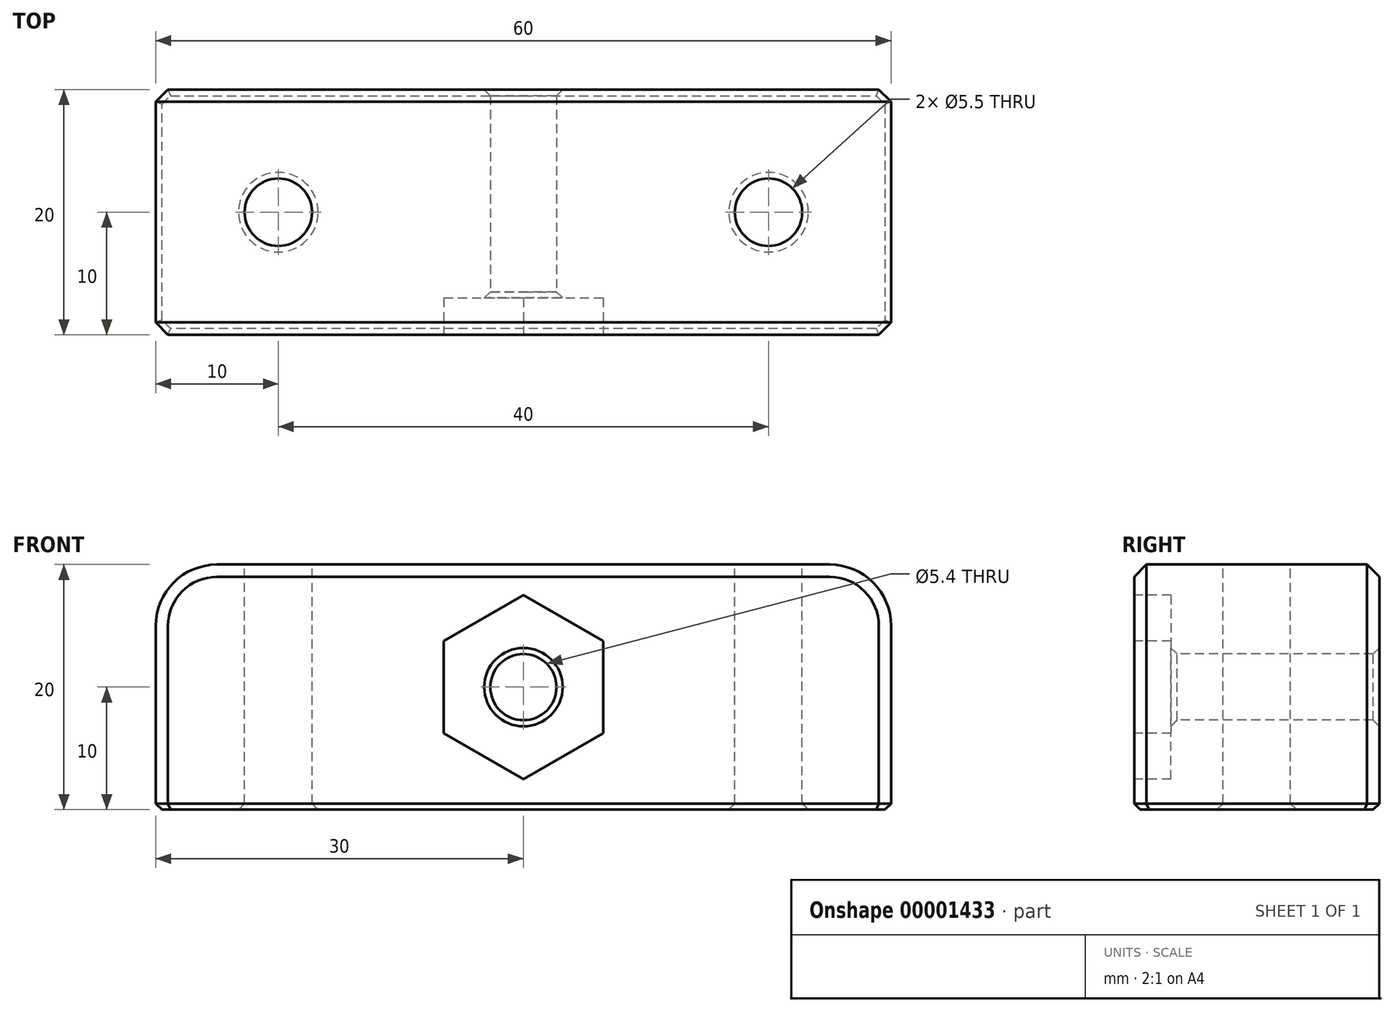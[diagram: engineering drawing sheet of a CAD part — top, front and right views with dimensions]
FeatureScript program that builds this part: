
annotation { "Feature Type Name" : "Feature", "Feature Type Description" : "" }
export const myFeature = defineFeature(function(context is Context, id is Id, definition is map)
    precondition{}
    {
        {
            var Q0;
            Q0=qCreatedBy(makeId("Top.planeOp"),FACE);
            var sketch = newSketch(context, id + "F0", { "sketchPlane" : qUnion([Q0])});
            skLineSegment(sketch, "E0.rect.bottom", {"start": v(30, 10) * mm, "end": v(-30, 10) * mm});
            skLineSegment(sketch, "E0.rect.top", {"start": v(30, -10) * mm, "end": v(-30, -10) * mm});
            skLineSegment(sketch, "E0.rect.left", {"start": v(30, 10) * mm, "end": v(30, -10) * mm});
            skLineSegment(sketch, "E0.rect.right", {"start": v(-30, 10) * mm, "end": v(-30, -10) * mm});
            skPoint(sketch, "E0.rect.middle", {"position": v(0, 0) * mm});
            skSolve(sketch);
        }
        {
            var Q0;
            Q0=makeQuery(id+"F0.imprint","IMPRINT",FACE,{"disambiguationData":[TD([[makeQuery(id+"F0.imprint","IMPRINT",EDGE,{"derivedFrom":sQuery(id+"F0.wireOp",EDGE,"E0.rect.bottom")}),1.0]])]});
            extrude(context, id + "F1", {"entities" : qUnion([Q0]), "depth" : 20 * mm});
        }
        {
            var Q0;
            Q0=makeQuery(id+"F1.opExtrude","SWEPT_FACE",FACE,{"disambiguationData":[OSD([sQuery(id+"F0.wireOp",EDGE,"E0.rect.top")])]});
            var sketch = newSketch(context, id + "F2", { "sketchPlane" : qUnion([Q0])});
            skLineSegment(sketch, "E1", {"start": v(0, 0) * mm, "end": v(0, 20) * mm, "construction": true});
            skCircle(sketch, "E2", {"center": v(0, 10) * mm, "radius": 2.7 * mm});
            skSolve(sketch);
        }
        {
            var Q0;
            Q0=makeQuery(id+"F2.imprint","IMPRINT",FACE,{"disambiguationData":[TD([[makeQuery(id+"F2.imprint","IMPRINT",EDGE,{"derivedFrom":sQuery(id+"F2.wireOp",EDGE,"E2")}),1.0]])]});
            extrude(context, id + "F3", {"entities" : qUnion([Q0]), "operationType" : NewBodyOperationType.REMOVE, "endBound" : BoundingType.THROUGH_ALL, "oppositeDirection" : true, "depth" : 25 * mm});
        }
        {
            var Q0;
            Q0=makeQuery(id+"F1.opExtrude","CAP_FACE",FACE,{"disambiguationData":[OSD([sQuery(id+"F0.wireOp",EDGE,"E0.rect.bottom"),sQuery(id+"F0.wireOp",EDGE,"E0.rect.top"),sQuery(id+"F0.wireOp",EDGE,"E0.rect.left"),sQuery(id+"F0.wireOp",EDGE,"E0.rect.right")])],"isStart":false});
            var sketch = newSketch(context, id + "F4", { "sketchPlane" : qUnion([Q0])});
            skLineSegment(sketch, "E3", {"start": v(30, 0) * mm, "end": v(20, 0) * mm, "construction": true});
            skLineSegment(sketch, "E4", {"start": v(20, 0) * mm, "end": v(-20, 0) * mm, "construction": true});
            skLineSegment(sketch, "E5", {"start": v(-20, 0) * mm, "end": v(-30, 0) * mm, "construction": true});
            skCircle(sketch, "E6", {"center": v(20, 0) * mm, "radius": 2.75 * mm});
            skCircle(sketch, "E7", {"center": v(-20, 0) * mm, "radius": 2.75 * mm});
            skSolve(sketch);
        }
        {
            var Q0;
            {Q0=qUnion([makeQuery(id+"F4.imprint","IMPRINT",FACE,{"disambiguationData":[TD([[makeQuery(id+"F4.imprint","IMPRINT",EDGE,{"derivedFrom":sQuery(id+"F4.wireOp",EDGE,"E6")}),1.0]])]}),makeQuery(id+"F4.imprint","IMPRINT",FACE,{"disambiguationData":[TD([[makeQuery(id+"F4.imprint","IMPRINT",EDGE,{"derivedFrom":sQuery(id+"F4.wireOp",EDGE,"E7")}),1.0]])]})]);}
            extrude(context, id + "F5", {"entities" : qUnion([Q0]), "operationType" : NewBodyOperationType.REMOVE, "endBound" : BoundingType.THROUGH_ALL, "oppositeDirection" : true, "depth" : 25 * mm});
        }
        {
            var Q0;
            Q0=makeQuery(id+"F1.opExtrude","CAP_EDGE",EDGE,{"disambiguationData":[OSD([sQuery(id+"F0.wireOp",EDGE,"E0.rect.right")])],"isStart":false});
            var Q1;
            Q1=makeQuery(id+"F1.opExtrude","CAP_EDGE",EDGE,{"disambiguationData":[OSD([sQuery(id+"F0.wireOp",EDGE,"E0.rect.left")])],"isStart":false});
            fillet(context, id + "F6", {"entities" : qUnion([Q0, Q1]), "radius" : 5 * mm, "tangentPropagation" : true, "allowEdgeOverflow" : false});
        }
        {
            var Q0;
            Q0=makeQuery(id+"F1.opExtrude","SWEPT_FACE",FACE,{"disambiguationData":[OSD([sQuery(id+"F0.wireOp",EDGE,"E0.rect.top")])]});
            var sketch = newSketch(context, id + "F7", { "sketchPlane" : qUnion([Q0])});
            skCircle(sketch, "E8.cCircle", {"center": v(0, 10) * mm, "radius": 6.5 * mm, "construction": true});
            skLineSegment(sketch, "E8.0", {"start": v(6.5, 13.75) * mm, "end": v(6.5, 6.25) * mm});
            skLineSegment(sketch, "E8.1", {"start": v(6.5, 6.25) * mm, "end": v(0, 2.5) * mm});
            skLineSegment(sketch, "E8.2", {"start": v(0, 2.5) * mm, "end": v(-6.5, 6.25) * mm});
            skLineSegment(sketch, "E8.3", {"start": v(-6.5, 6.25) * mm, "end": v(-6.5, 13.75) * mm});
            skLineSegment(sketch, "E8.4", {"start": v(-6.5, 13.75) * mm, "end": v(0, 17.5) * mm});
            skLineSegment(sketch, "E8.5", {"start": v(0, 17.5) * mm, "end": v(6.5, 13.75) * mm});
            skPoint(sketch, "E8.0.midPoint", {"position": v(6.5, 10) * mm});
            skSolve(sketch);
        }
        {
            var Q0;
            Q0 = qSketchRegion(id + "F7", true);
            extrude(context, id + "F8", {"entities" : qUnion([Q0]), "operationType" : NewBodyOperationType.REMOVE, "oppositeDirection" : true, "depth" : 3 * mm});
        }
        {
            var Q0;
            Q0=makeQuery(id+"F1.opExtrude","CAP_EDGE",EDGE,{"disambiguationData":[OSD([sQuery(id+"F0.wireOp",EDGE,"E0.rect.top")])],"isStart":false});
            var Q1;
            Q1=makeQuery(id+"F1.opExtrude","CAP_EDGE",EDGE,{"disambiguationData":[OSD([sQuery(id+"F0.wireOp",EDGE,"E0.rect.bottom")])],"isStart":false});
            chamfer(context, id + "F9", {"entities" : qUnion([Q0, Q1]), "width" : 1 * mm, "tangentPropagation" : true});
        }
        {
            var Q0;
            Q0=makeQuery(id+"F5.boolean.opBoolean","COPY",EDGE,{"derivedFrom":makeQuery(id+"F5.opExtrude","CAP_EDGE",EDGE,{"disambiguationData":[OSD([sQuery(id+"F4.wireOp",EDGE,"E7")])],"isStart":true})});
            var Q1;
            Q1=makeQuery(id+"F5.boolean.opBoolean","COPY",EDGE,{"derivedFrom":makeQuery(id+"F5.opExtrude","CAP_EDGE",EDGE,{"disambiguationData":[OSD([sQuery(id+"F4.wireOp",EDGE,"E6")])],"isStart":true})});
            var Q2;
            Q2=makeQuery(id+"F5.boolean.opBoolean","INTERSECT",EDGE,{"derivedFrom":[makeQuery(id+"F1.opExtrude","CAP_FACE",FACE,{"disambiguationData":[OSD([sQuery(id+"F0.wireOp",EDGE,"E0.rect.bottom"),sQuery(id+"F0.wireOp",EDGE,"E0.rect.top"),sQuery(id+"F0.wireOp",EDGE,"E0.rect.left"),sQuery(id+"F0.wireOp",EDGE,"E0.rect.right")])],"isStart":true}),makeQuery(id+"F5.opExtrude","SWEPT_FACE",FACE,{"disambiguationData":[OSD([sQuery(id+"F4.wireOp",EDGE,"E7")])]})]});
            var Q3;
            Q3=makeQuery(id+"F5.boolean.opBoolean","INTERSECT",EDGE,{"derivedFrom":[makeQuery(id+"F1.opExtrude","CAP_FACE",FACE,{"disambiguationData":[OSD([sQuery(id+"F0.wireOp",EDGE,"E0.rect.bottom"),sQuery(id+"F0.wireOp",EDGE,"E0.rect.top"),sQuery(id+"F0.wireOp",EDGE,"E0.rect.left"),sQuery(id+"F0.wireOp",EDGE,"E0.rect.right")])],"isStart":true}),makeQuery(id+"F5.opExtrude","SWEPT_FACE",FACE,{"disambiguationData":[OSD([sQuery(id+"F4.wireOp",EDGE,"E6")])]})]});
            chamfer(context, id + "F10", {"entities" : qUnion([Q0, Q1, Q2, Q3]), "width" : 0.5 * mm, "tangentPropagation" : true});
        }
        {
            var Q0;
            Q0=makeQuery(id+"F1.opExtrude","CAP_EDGE",EDGE,{"disambiguationData":[OSD([sQuery(id+"F0.wireOp",EDGE,"E0.rect.top")])],"isStart":true});
            var Q1;
            {var subQ0=sQuery(id+"F0.wireOp",EDGE,"E0.rect.left");var subQ1=sQuery(id+"F0.wireOp",EDGE,"E0.rect.top");Q1=makeQuery(id+"F9.opChamfer","BLEND_EDGE",EDGE,{"blendedFrom":[makeQuery(id+"F1.opExtrude","SWEPT_EDGE",EDGE,{"disambiguationData":[OSD([subQ1,subQ0])]}),makeQuery(id+"F1.opExtrude","CAP_FACE",FACE,{"disambiguationData":[OSD([sQuery(id+"F0.wireOp",EDGE,"E0.rect.bottom"),subQ1,subQ0,sQuery(id+"F0.wireOp",EDGE,"E0.rect.right")])],"isStart":true})],"blendedInto":[makeQuery(id+"F1.opExtrude","CAP_FACE",FACE,{"disambiguationData":[OSD([sQuery(id+"F0.wireOp",EDGE,"E0.rect.bottom"),subQ1,subQ0,sQuery(id+"F0.wireOp",EDGE,"E0.rect.right")])],"isStart":true})]});}
            var Q2;
            Q2=makeQuery(id+"F1.opExtrude","CAP_EDGE",EDGE,{"disambiguationData":[OSD([sQuery(id+"F0.wireOp",EDGE,"E0.rect.left")])],"isStart":true});
            var Q3;
            {var subQ0=sQuery(id+"F0.wireOp",EDGE,"E0.rect.left");var subQ1=sQuery(id+"F0.wireOp",EDGE,"E0.rect.bottom");Q3=makeQuery(id+"F9.opChamfer","BLEND_EDGE",EDGE,{"blendedFrom":[makeQuery(id+"F1.opExtrude","SWEPT_EDGE",EDGE,{"disambiguationData":[OSD([subQ1,subQ0])]}),makeQuery(id+"F1.opExtrude","CAP_FACE",FACE,{"disambiguationData":[OSD([subQ1,sQuery(id+"F0.wireOp",EDGE,"E0.rect.top"),subQ0,sQuery(id+"F0.wireOp",EDGE,"E0.rect.right")])],"isStart":true})],"blendedInto":[makeQuery(id+"F1.opExtrude","CAP_FACE",FACE,{"disambiguationData":[OSD([subQ1,sQuery(id+"F0.wireOp",EDGE,"E0.rect.top"),subQ0,sQuery(id+"F0.wireOp",EDGE,"E0.rect.right")])],"isStart":true})]});}
            var Q4;
            Q4=makeQuery(id+"F1.opExtrude","CAP_EDGE",EDGE,{"disambiguationData":[OSD([sQuery(id+"F0.wireOp",EDGE,"E0.rect.bottom")])],"isStart":true});
            var Q5;
            {var subQ0=sQuery(id+"F0.wireOp",EDGE,"E0.rect.right");var subQ1=sQuery(id+"F0.wireOp",EDGE,"E0.rect.bottom");Q5=makeQuery(id+"F9.opChamfer","BLEND_EDGE",EDGE,{"blendedFrom":[makeQuery(id+"F1.opExtrude","SWEPT_EDGE",EDGE,{"disambiguationData":[OSD([subQ1,subQ0])]}),makeQuery(id+"F1.opExtrude","CAP_FACE",FACE,{"disambiguationData":[OSD([subQ1,sQuery(id+"F0.wireOp",EDGE,"E0.rect.top"),sQuery(id+"F0.wireOp",EDGE,"E0.rect.left"),subQ0])],"isStart":true})],"blendedInto":[makeQuery(id+"F1.opExtrude","CAP_FACE",FACE,{"disambiguationData":[OSD([subQ1,sQuery(id+"F0.wireOp",EDGE,"E0.rect.top"),sQuery(id+"F0.wireOp",EDGE,"E0.rect.left"),subQ0])],"isStart":true})]});}
            var Q6;
            Q6=makeQuery(id+"F1.opExtrude","CAP_EDGE",EDGE,{"disambiguationData":[OSD([sQuery(id+"F0.wireOp",EDGE,"E0.rect.right")])],"isStart":true});
            var Q7;
            {var subQ0=sQuery(id+"F0.wireOp",EDGE,"E0.rect.right");var subQ1=sQuery(id+"F0.wireOp",EDGE,"E0.rect.top");Q7=makeQuery(id+"F9.opChamfer","BLEND_EDGE",EDGE,{"blendedFrom":[makeQuery(id+"F1.opExtrude","SWEPT_EDGE",EDGE,{"disambiguationData":[OSD([subQ1,subQ0])]}),makeQuery(id+"F1.opExtrude","CAP_FACE",FACE,{"disambiguationData":[OSD([sQuery(id+"F0.wireOp",EDGE,"E0.rect.bottom"),subQ1,sQuery(id+"F0.wireOp",EDGE,"E0.rect.left"),subQ0])],"isStart":true})],"blendedInto":[makeQuery(id+"F1.opExtrude","CAP_FACE",FACE,{"disambiguationData":[OSD([sQuery(id+"F0.wireOp",EDGE,"E0.rect.bottom"),subQ1,sQuery(id+"F0.wireOp",EDGE,"E0.rect.left"),subQ0])],"isStart":true})]});}
            chamfer(context, id + "F11", {"entities" : qUnion([Q0, Q1, Q2, Q3, Q4, Q5, Q6, Q7]), "width" : 0.5 * mm, "tangentPropagation" : true});
        }
        {
            var Q0;
            Q0=makeQuery(id+"F8.boolean.opBoolean","INTERSECT",EDGE,{"derivedFrom":[makeQuery(id+"F3.boolean.opBoolean","COPY",FACE,{"derivedFrom":makeQuery(id+"F3.opExtrude","SWEPT_FACE",FACE,{"disambiguationData":[OSD([sQuery(id+"F2.wireOp",EDGE,"E2")])]})}),makeQuery(id+"F8.opExtrude","CAP_FACE",FACE,{"disambiguationData":[OSD([sQuery(id+"F7.wireOp",EDGE,"E8.0"),sQuery(id+"F7.wireOp",EDGE,"E8.1"),sQuery(id+"F7.wireOp",EDGE,"E8.2"),sQuery(id+"F7.wireOp",EDGE,"E8.3"),sQuery(id+"F7.wireOp",EDGE,"E8.4"),sQuery(id+"F7.wireOp",EDGE,"E8.5")])],"isStart":false})]});
            var Q1;
            Q1=makeQuery(id+"F3.boolean.opBoolean","INTERSECT",EDGE,{"derivedFrom":[makeQuery(id+"F1.opExtrude","SWEPT_FACE",FACE,{"disambiguationData":[OSD([sQuery(id+"F0.wireOp",EDGE,"E0.rect.bottom")])]}),makeQuery(id+"F3.opExtrude","SWEPT_FACE",FACE,{"disambiguationData":[OSD([sQuery(id+"F2.wireOp",EDGE,"E2")])]})]});
            chamfer(context, id + "F12", {"entities" : qUnion([Q0, Q1]), "width" : 0.5 * mm, "tangentPropagation" : true});
        }
    });
